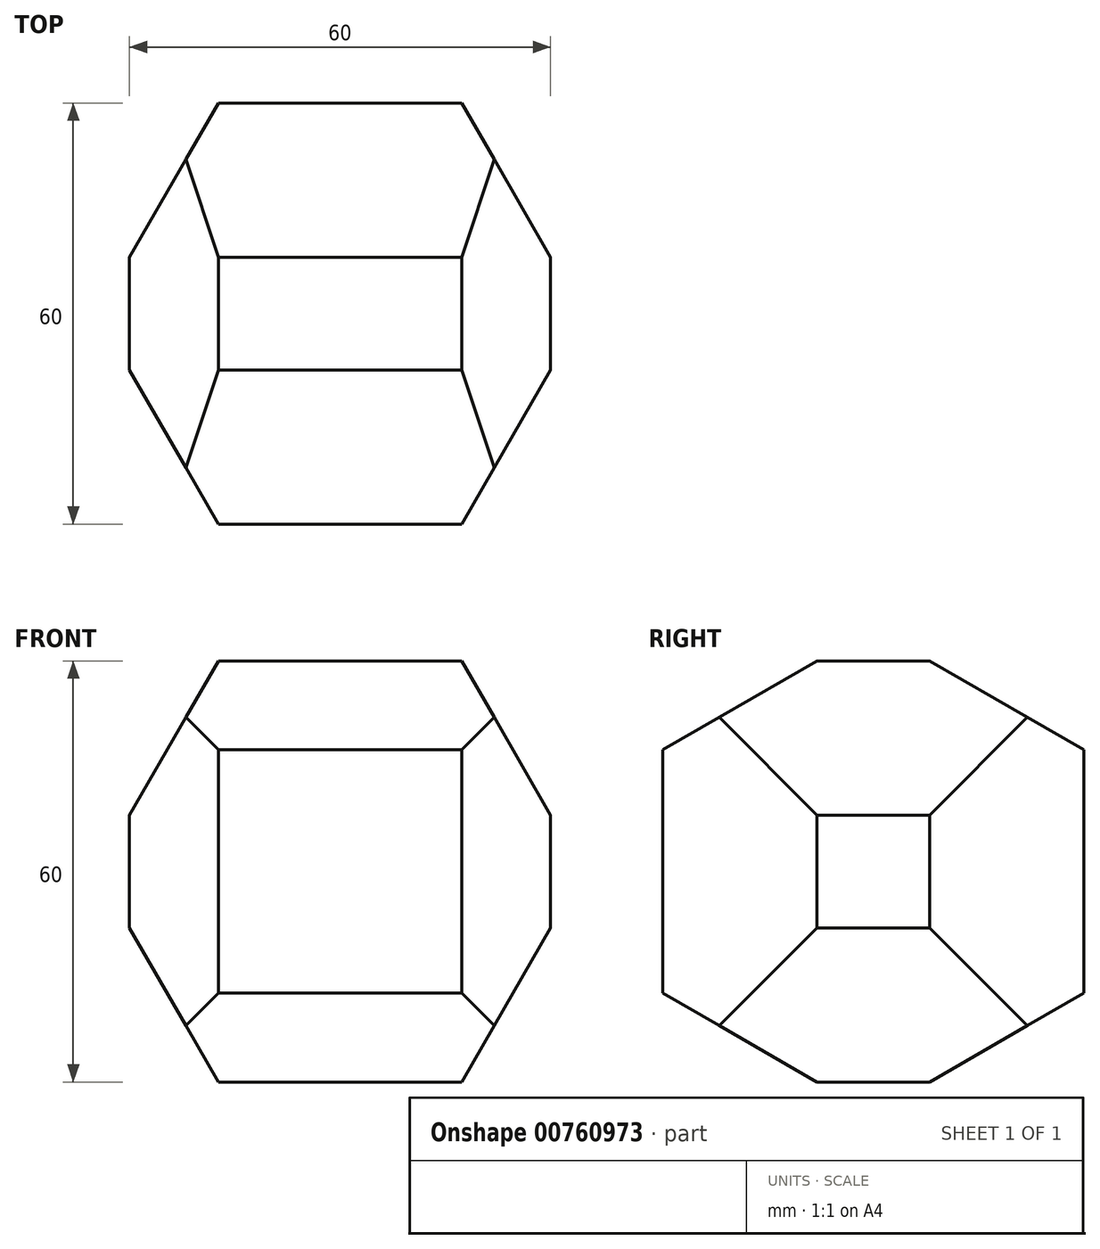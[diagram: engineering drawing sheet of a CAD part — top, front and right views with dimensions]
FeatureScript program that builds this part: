
annotation { "Feature Type Name" : "Feature", "Feature Type Description" : "" }
export const myFeature = defineFeature(function(context is Context, id is Id, definition is map)
    precondition{}
    {
        {
            var Q0;
            Q0=qCreatedBy(makeId("Top.planeOp"),FACE);
            var sketch = newSketch(context, id + "F0", { "sketchPlane" : qUnion([Q0])});
            skCircle(sketch, "E0.cCircle", {"center": v(0, 0) * mm, "radius": 30 * mm, "construction": true});
            skLineSegment(sketch, "E0.0", {"start": v(-17.32, 30) * mm, "end": v(17.32, 30) * mm});
            skLineSegment(sketch, "E0.1", {"start": v(17.32, 30) * mm, "end": v(34.64, 0) * mm});
            skLineSegment(sketch, "E0.2", {"start": v(34.64, 0) * mm, "end": v(17.32, -30) * mm});
            skLineSegment(sketch, "E0.3", {"start": v(17.32, -30) * mm, "end": v(-17.32, -30) * mm});
            skLineSegment(sketch, "E0.4", {"start": v(-17.32, -30) * mm, "end": v(-34.64, 0) * mm});
            skLineSegment(sketch, "E0.5", {"start": v(-34.64, 0) * mm, "end": v(-17.32, 30) * mm});
            skPoint(sketch, "E0.0.midPoint", {"position": v(0, 30) * mm});
            skSolve(sketch);
        }
        {
            var Q0;
            Q0=qCreatedBy(makeId("Right.planeOp"),FACE);
            var sketch = newSketch(context, id + "F1", { "sketchPlane" : qUnion([Q0])});
            skCircle(sketch, "E1.cCircle", {"center": v(0, 0) * mm, "radius": 30 * mm, "construction": true});
            skLineSegment(sketch, "E1.0", {"start": v(30, 17.32) * mm, "end": v(30, -17.32) * mm});
            skLineSegment(sketch, "E1.1", {"start": v(30, -17.32) * mm, "end": v(0, -34.64) * mm});
            skLineSegment(sketch, "E1.2", {"start": v(0, -34.64) * mm, "end": v(-30, -17.32) * mm});
            skLineSegment(sketch, "E1.3", {"start": v(-30, -17.32) * mm, "end": v(-30, 17.32) * mm});
            skLineSegment(sketch, "E1.4", {"start": v(-30, 17.32) * mm, "end": v(0, 34.64) * mm});
            skLineSegment(sketch, "E1.5", {"start": v(0, 34.64) * mm, "end": v(30, 17.32) * mm});
            skPoint(sketch, "E1.0.midPoint", {"position": v(30, 0) * mm});
            skSolve(sketch);
        }
        {
            var Q0;
            Q0=qCreatedBy(makeId("Front.planeOp"),FACE);
            var sketch = newSketch(context, id + "F2", { "sketchPlane" : qUnion([Q0])});
            skCircle(sketch, "E2.cCircle", {"center": v(0, 0) * mm, "radius": 30 * mm, "construction": true});
            skLineSegment(sketch, "E2.0", {"start": v(-17.32, 30) * mm, "end": v(17.32, 30) * mm});
            skLineSegment(sketch, "E2.1", {"start": v(17.32, 30) * mm, "end": v(34.64, 0) * mm});
            skLineSegment(sketch, "E2.2", {"start": v(34.64, 0) * mm, "end": v(17.32, -30) * mm});
            skLineSegment(sketch, "E2.3", {"start": v(17.32, -30) * mm, "end": v(-17.32, -30) * mm});
            skLineSegment(sketch, "E2.4", {"start": v(-17.32, -30) * mm, "end": v(-34.64, 0) * mm});
            skLineSegment(sketch, "E2.5", {"start": v(-34.64, 0) * mm, "end": v(-17.32, 30) * mm});
            skPoint(sketch, "E2.0.midPoint", {"position": v(0, 30) * mm});
            skSolve(sketch);
        }
        {
            var Q0;
            Q0=qSketchRegion(id+"F0",true);
            extrude(context, id + "F3", {"entities" : qUnion([Q0]), "endBound" : BoundingType.SYMMETRIC, "depth" : 60 * mm});
        }
        {
            var Q0;
            Q0=qSketchRegion(id+"F1",true);
            extrude(context, id + "F4", {"entities" : qUnion([Q0]), "operationType" : NewBodyOperationType.INTERSECT, "endBound" : BoundingType.SYMMETRIC, "depth" : 60 * mm});
        }
        {
            var Q0;
            Q0=qSketchRegion(id+"F2",true);
            extrude(context, id + "F5", {"entities" : qUnion([Q0]), "operationType" : NewBodyOperationType.INTERSECT, "endBound" : BoundingType.SYMMETRIC, "depth" : 60 * mm});
        }
    });
